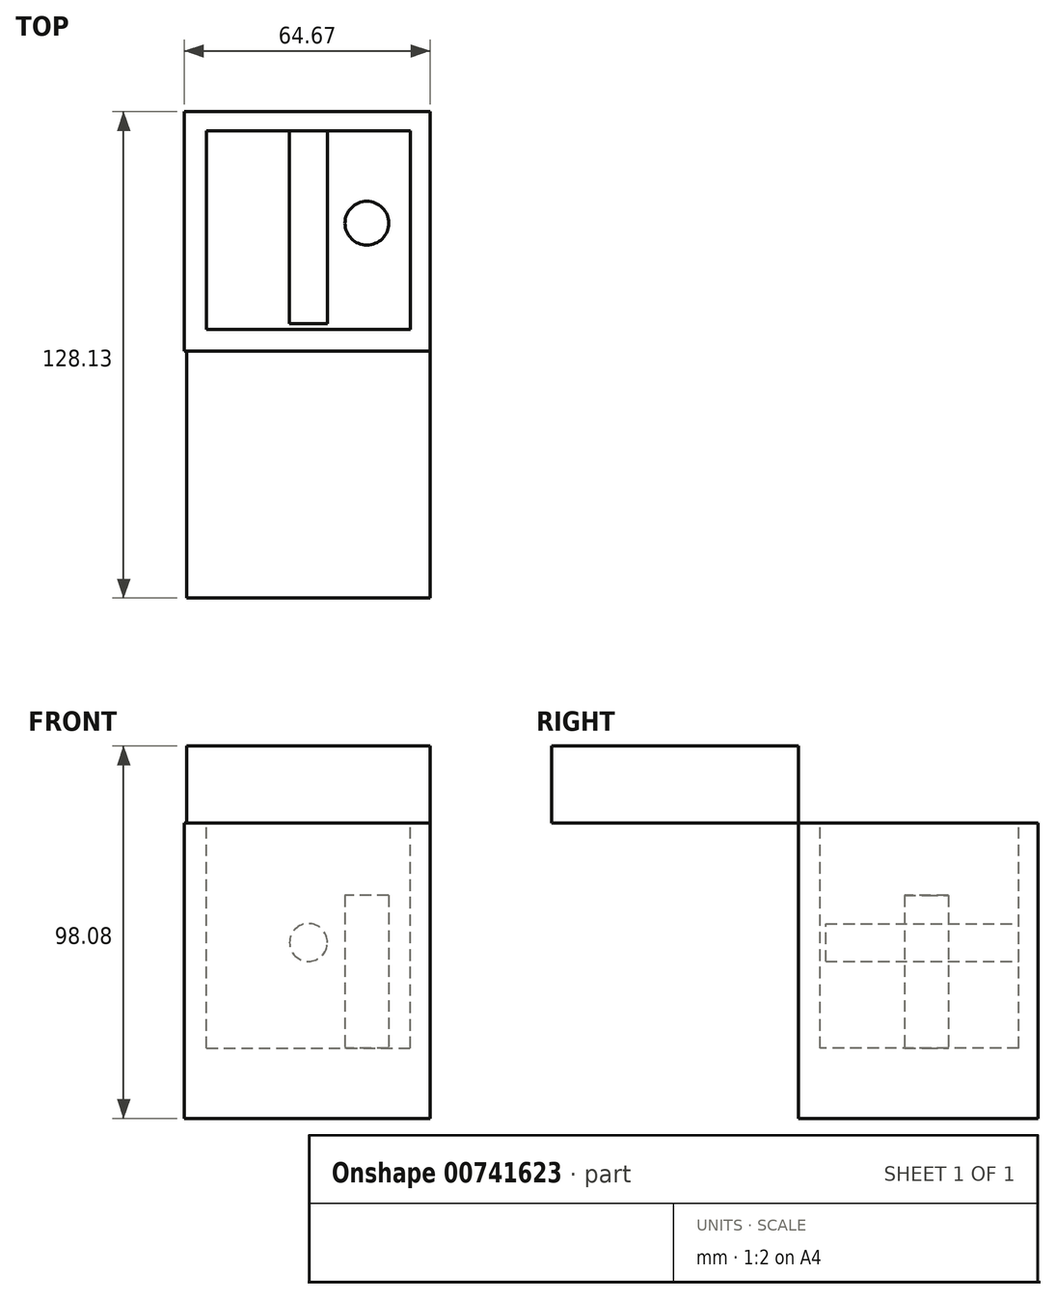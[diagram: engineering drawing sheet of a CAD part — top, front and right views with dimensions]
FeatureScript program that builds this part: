
annotation { "Feature Type Name" : "Feature", "Feature Type Description" : "" }
export const myFeature = defineFeature(function(context is Context, id is Id, definition is map)
    precondition{}
    {
        {
            var Q0;
            Q0=qCreatedBy(makeId("Top.planeOp"),FACE);
            var sketch = newSketch(context, id + "F0", { "sketchPlane" : qUnion([Q0])});
            skLineSegment(sketch, "E0.bottom", {"start": v(-64.67, 63.05) * mm, "end": v(0, 63.05) * mm});
            skLineSegment(sketch, "E0.top", {"start": v(-64.67, 0) * mm, "end": v(0, 0) * mm});
            skLineSegment(sketch, "E0.left", {"start": v(-64.67, 63.05) * mm, "end": v(-64.67, 0) * mm});
            skLineSegment(sketch, "E0.right", {"start": v(0, 63.05) * mm, "end": v(0, 0) * mm});
            skSolve(sketch);
        }
        {
            var Q0;
            Q0 = qSketchRegion(id + "F0", true);
            extrude(context, id + "F1", {"entities" : qUnion([Q0]), "oppositeDirection" : true, "depth" : 77.76 * mm, "offsetDistance" : 25.4 * mm});
        }
        {
            var Q0;
            Q0=makeQuery(id+"F1.opExtrude","CAP_FACE",FACE,{"disambiguationData":[OSD([sQuery(id+"F0.wireOp",EDGE,"E0.bottom"),sQuery(id+"F0.wireOp",EDGE,"E0.top"),sQuery(id+"F0.wireOp",EDGE,"E0.left"),sQuery(id+"F0.wireOp",EDGE,"E0.right")])],"isStart":true});
            var sketch = newSketch(context, id + "F2", { "sketchPlane" : qUnion([Q0])});
            skLineSegment(sketch, "E1.bottom", {"start": v(-58.87, 58) * mm, "end": v(-5.15, 58) * mm});
            skLineSegment(sketch, "E1.top", {"start": v(-58.87, 5.67) * mm, "end": v(-5.15, 5.67) * mm});
            skLineSegment(sketch, "E1.left", {"start": v(-58.87, 58) * mm, "end": v(-58.87, 5.67) * mm});
            skLineSegment(sketch, "E1.right", {"start": v(-5.15, 58) * mm, "end": v(-5.15, 5.67) * mm});
            skSolve(sketch);
        }
        {
            var Q0;
            Q0 = qSketchRegion(id + "F2", true);
            extrude(context, id + "F3", {"entities" : qUnion([Q0]), "operationType" : NewBodyOperationType.REMOVE, "oppositeDirection" : true, "depth" : 59.24 * mm, "offsetDistance" : 25.4 * mm});
        }
        {
            var Q0;
            Q0=makeQuery(id+"F3.boolean.opBoolean","COPY",FACE,{"derivedFrom":makeQuery(id+"F3.opExtrude","SWEPT_FACE",FACE,{"disambiguationData":[OSD([sQuery(id+"F2.wireOp",EDGE,"E1.bottom")])]})});
            var sketch = newSketch(context, id + "F4", { "sketchPlane" : qUnion([Q0])});
            skCircle(sketch, "E2", {"center": v(-32.01, -31.45) * mm, "radius": 4.98 * mm});
            skPoint(sketch, "E2.centerSnap0", {"position": v(-32.01, 0) * mm});
            skSolve(sketch);
        }
        {
            var Q0;
            Q0 = qSketchRegion(id + "F4", true);
            extrude(context, id + "F5", {"entities" : qUnion([Q0]), "operationType" : NewBodyOperationType.ADD, "depth" : 50.8 * mm, "offsetDistance" : 25.4 * mm});
        }
        {
            var Q0;
            Q0=makeQuery(id+"F3.boolean.opBoolean","COPY",FACE,{"derivedFrom":makeQuery(id+"F3.opExtrude","CAP_FACE",FACE,{"disambiguationData":[OSD([sQuery(id+"F2.wireOp",EDGE,"E1.bottom"),sQuery(id+"F2.wireOp",EDGE,"E1.top"),sQuery(id+"F2.wireOp",EDGE,"E1.left"),sQuery(id+"F2.wireOp",EDGE,"E1.right")])],"isStart":false})});
            var sketch = newSketch(context, id + "F6", { "sketchPlane" : qUnion([Q0])});
            skCircle(sketch, "E3", {"center": v(-16.62, 33.67) * mm, "radius": 5.76 * mm});
            skSolve(sketch);
        }
        {
            var Q0;
            Q0 = qSketchRegion(id + "F6", true);
            extrude(context, id + "F7", {"entities" : qUnion([Q0]), "operationType" : NewBodyOperationType.ADD, "depth" : 40.2 * mm, "offsetDistance" : 25.4 * mm});
        }
        {
            var Q0;
            Q0=qCreatedBy(makeId("Top.planeOp"),FACE);
            var sketch = newSketch(context, id + "F8", { "sketchPlane" : qUnion([Q0])});
            skLineSegment(sketch, "E4.bottom", {"start": v(-64.1, -65.08) * mm, "end": v(0, -65.08) * mm});
            skLineSegment(sketch, "E4.top", {"start": v(-64.1, 0) * mm, "end": v(0, 0) * mm});
            skLineSegment(sketch, "E4.left", {"start": v(-64.1, -65.08) * mm, "end": v(-64.1, 0) * mm});
            skLineSegment(sketch, "E4.right", {"start": v(0, -65.08) * mm, "end": v(0, 0) * mm});
            skSolve(sketch);
        }
        {
            var Q0;
            Q0 = qSketchRegion(id + "F8", true);
            extrude(context, id + "F9", {"entities" : qUnion([Q0]), "depth" : 20.32 * mm, "offsetDistance" : 25.4 * mm});
        }
    });
